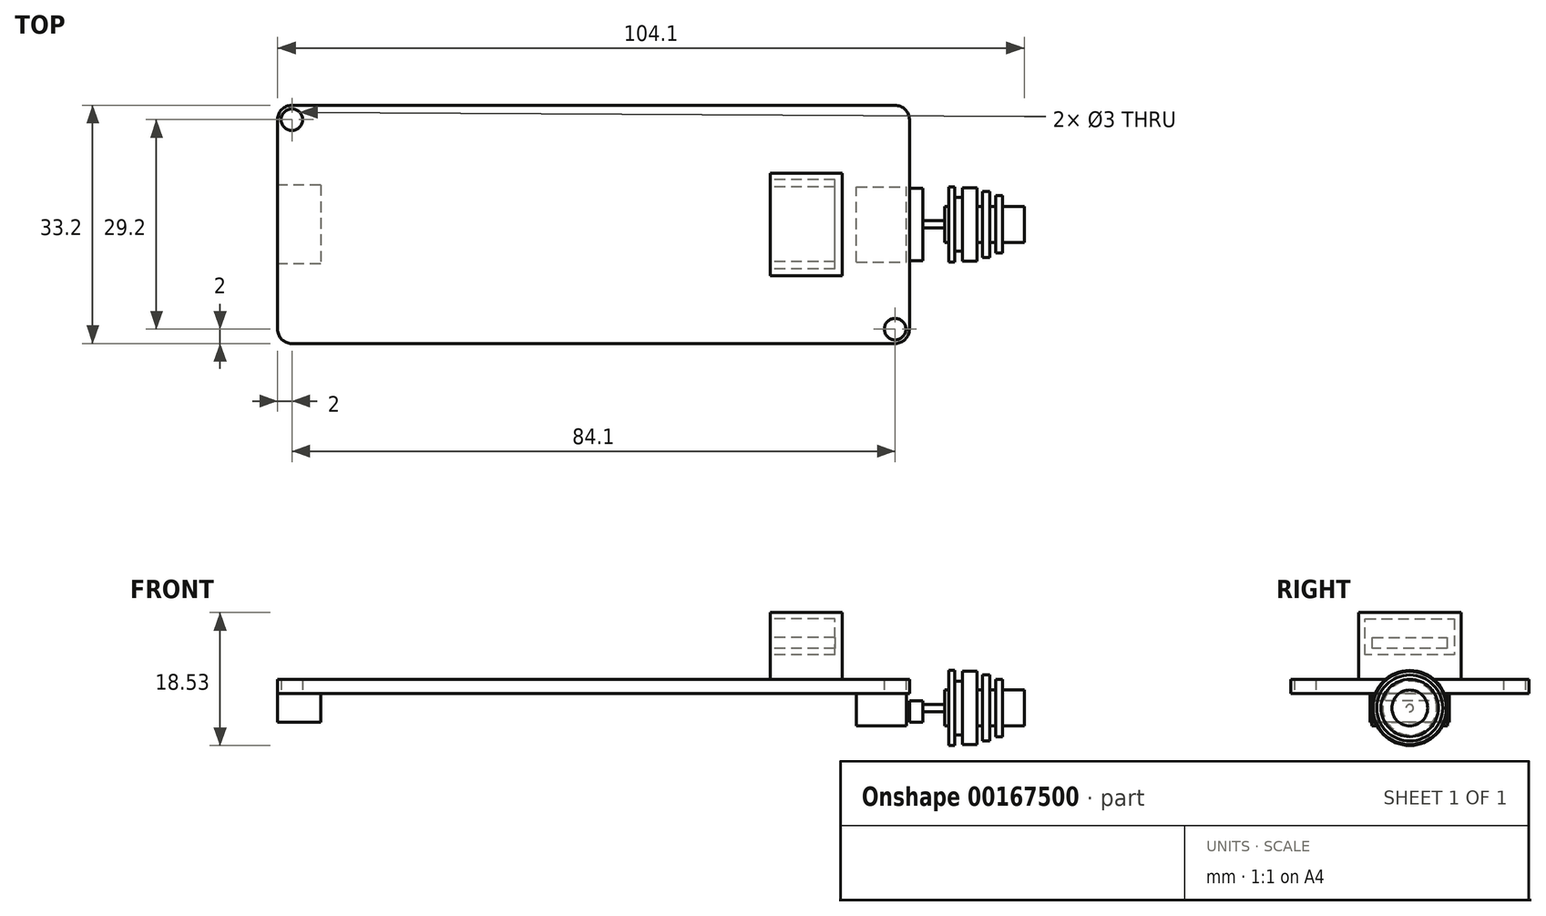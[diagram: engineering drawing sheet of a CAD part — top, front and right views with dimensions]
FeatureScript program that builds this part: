
annotation { "Feature Type Name" : "Feature", "Feature Type Description" : "" }
export const myFeature = defineFeature(function(context is Context, id is Id, definition is map)
    precondition{}
    {
        {
            var Q0;
            Q0=qCreatedBy(makeId("Top.planeOp"),FACE);
            var sketch = newSketch(context, id + "F0", { "sketchPlane" : qUnion([Q0])});
            skLineSegment(sketch, "E0.bottom", {"start": v(2, 0) * mm, "end": v(86.1, 0) * mm});
            skLineSegment(sketch, "E0.top", {"start": v(2, -33.2) * mm, "end": v(86.1, -33.2) * mm});
            skLineSegment(sketch, "E0.left", {"start": v(0, -2) * mm, "end": v(0, -31.2) * mm});
            skLineSegment(sketch, "E0.right", {"start": v(88.1, -2) * mm, "end": v(88.1, -31.2) * mm});
            skPoint(sketch, "E1.visualSharp", {"position": v(88.1, 0) * mm});
            skArc(sketch, "E1.filletArc", {"start": v(88.1, -2) * mm, "mid": v(87.51, -0.59) * mm, "end": v(86.1, 0) * mm});
            skPoint(sketch, "E2.visualSharp", {"position": v(88.1, -33.2) * mm});
            skArc(sketch, "E2.filletArc", {"start": v(86.1, -33.2) * mm, "mid": v(87.51, -32.61) * mm, "end": v(88.1, -31.2) * mm});
            skPoint(sketch, "E3.visualSharp", {"position": v(0, -33.2) * mm});
            skArc(sketch, "E3.filletArc", {"start": v(0, -31.2) * mm, "mid": v(0.59, -32.61) * mm, "end": v(2, -33.2) * mm});
            skPoint(sketch, "E4.visualSharp", {"position": v(0, 0) * mm});
            skArc(sketch, "E4.filletArc", {"start": v(2, 0) * mm, "mid": v(0.59, -0.59) * mm, "end": v(0, -2) * mm});
            skCircle(sketch, "E5", {"center": v(2, -2) * mm, "radius": 1.5 * mm});
            skCircle(sketch, "E6", {"center": v(86.1, -31.2) * mm, "radius": 1.5 * mm});
            skLineSegment(sketch, "E7", {"start": v(0, -16.6) * mm, "end": v(88.1, -16.6) * mm, "construction": true});
            skLineSegment(sketch, "E8", {"start": v(44.05, 0) * mm, "end": v(44.05, -33.2) * mm, "construction": true});
            skSolve(sketch);
        }
        {
            var Q0;
            Q0=makeQuery(id+"F0.imprint","IMPRINT",FACE,{"disambiguationData":[TD([[makeQuery(id+"F0.imprint","IMPRINT",EDGE,{"derivedFrom":sQuery(id+"F0.wireOp",EDGE,"E0.bottom")}),-1.0]])]});
            extrude(context, id + "F1", {"entities" : qUnion([Q0]), "depth" : 2 * mm});
        }
        {
            var Q0;
            Q0=makeQuery(id+"F1.opExtrude","CAP_FACE",FACE,{"disambiguationData":[OSD([sQuery(id+"F0.wireOp",EDGE,"E0.bottom"),sQuery(id+"F0.wireOp",EDGE,"E0.top"),sQuery(id+"F0.wireOp",EDGE,"E0.left"),sQuery(id+"F0.wireOp",EDGE,"E0.right"),sQuery(id+"F0.wireOp",EDGE,"E1.filletArc"),sQuery(id+"F0.wireOp",EDGE,"E2.filletArc"),sQuery(id+"F0.wireOp",EDGE,"E3.filletArc"),sQuery(id+"F0.wireOp",EDGE,"E4.filletArc"),sQuery(id+"F0.wireOp",EDGE,"E5"),sQuery(id+"F0.wireOp",EDGE,"E6")])],"isStart":false});
            var sketch = newSketch(context, id + "F2", { "sketchPlane" : qUnion([Q0])});
            skLineSegment(sketch, "E9.bottom", {"start": v(68.7, -9.45) * mm, "end": v(78.7, -9.45) * mm});
            skLineSegment(sketch, "E9.top", {"start": v(68.7, -23.75) * mm, "end": v(78.7, -23.75) * mm});
            skLineSegment(sketch, "E9.left", {"start": v(68.7, -9.45) * mm, "end": v(68.7, -23.75) * mm});
            skLineSegment(sketch, "E9.right", {"start": v(78.7, -9.45) * mm, "end": v(78.7, -23.75) * mm});
            skPoint(sketch, "E10", {"position": v(78.7, -16.6) * mm});
            skSolve(sketch);
        }
        {
            var Q0;
            Q0=makeQuery(id+"F2.imprint","IMPRINT",FACE,{"disambiguationData":[TD([[makeQuery(id+"F2.imprint","IMPRINT",EDGE,{"derivedFrom":sQuery(id+"F2.wireOp",EDGE,"E9.bottom")}),-1.0]])]});
            extrude(context, id + "F3", {"entities" : qUnion([Q0]), "depth" : 9.3 * mm});
        }
        {
            var Q0;
            Q0=makeQuery(id+"F3.opExtrude","SWEPT_FACE",FACE,{"disambiguationData":[OSD([sQuery(id+"F2.wireOp",EDGE,"E9.left")])]});
            var sketch = newSketch(context, id + "F4", { "sketchPlane" : qUnion([Q0])});
            skLineSegment(sketch, "E11.0.0", {"start": v(11.4, 7.8) * mm, "end": v(11.4, 6.3) * mm});
            skLineSegment(sketch, "E12.0.0", {"start": v(22.83, 10.4) * mm, "end": v(10.38, 10.4) * mm});
            skLineSegment(sketch, "E12.0.1", {"start": v(10.38, 10.4) * mm, "end": v(10.38, 5.4) * mm});
            skLineSegment(sketch, "E12.0.2", {"start": v(10.38, 5.4) * mm, "end": v(22.83, 5.4) * mm});
            skLineSegment(sketch, "E12.0.3", {"start": v(22.83, 5.4) * mm, "end": v(22.83, 10.4) * mm});
            skLineSegment(sketch, "E11.0.1", {"start": v(11.4, 6.3) * mm, "end": v(21.8, 6.3) * mm});
            skLineSegment(sketch, "E11.0.2", {"start": v(21.8, 6.3) * mm, "end": v(21.8, 7.8) * mm});
            skLineSegment(sketch, "E11.0.3", {"start": v(21.8, 7.8) * mm, "end": v(11.4, 7.8) * mm});
            skLineSegment(sketch, "E13.0", {"start": v(9.45, 11.3) * mm, "end": v(23.75, 11.3) * mm, "construction": true});
            skLineSegment(sketch, "E14.0", {"start": v(9.45, 11.3) * mm, "end": v(9.45, 2) * mm, "construction": true});
            skLineSegment(sketch, "E15.0", {"start": v(23.75, 11.3) * mm, "end": v(23.75, 2) * mm, "construction": true});
            skLineSegment(sketch, "E16.0", {"start": v(9.45, 2) * mm, "end": v(23.75, 2) * mm, "construction": true});
            skSolve(sketch);
        }
        {
            var Q0;
            Q0=makeQuery(id+"F4.imprint","IMPRINT",FACE,{"disambiguationData":[TD([[makeQuery(id+"F4.imprint","IMPRINT",EDGE,{"derivedFrom":sQuery(id+"F4.wireOp",EDGE,"E11.0.0")}),-1.0]])]});
            extrude(context, id + "F5", {"entities" : qUnion([Q0]), "operationType" : NewBodyOperationType.REMOVE, "oppositeDirection" : true, "depth" : 9 * mm});
        }
        {
            var Q0;
            Q0=makeQuery(id+"F1.opExtrude","CAP_FACE",FACE,{"disambiguationData":[OSD([sQuery(id+"F0.wireOp",EDGE,"E0.bottom"),sQuery(id+"F0.wireOp",EDGE,"E0.top"),sQuery(id+"F0.wireOp",EDGE,"E0.left"),sQuery(id+"F0.wireOp",EDGE,"E0.right"),sQuery(id+"F0.wireOp",EDGE,"E1.filletArc"),sQuery(id+"F0.wireOp",EDGE,"E2.filletArc"),sQuery(id+"F0.wireOp",EDGE,"E3.filletArc"),sQuery(id+"F0.wireOp",EDGE,"E4.filletArc"),sQuery(id+"F0.wireOp",EDGE,"E5"),sQuery(id+"F0.wireOp",EDGE,"E6")])],"isStart":true});
            var sketch = newSketch(context, id + "F6", { "sketchPlane" : qUnion([Q0])});
            skLineSegment(sketch, "E17.bottom", {"start": v(80.7, 21.85) * mm, "end": v(87.7, 21.85) * mm});
            skLineSegment(sketch, "E17.top", {"start": v(80.7, 11.35) * mm, "end": v(87.7, 11.35) * mm});
            skLineSegment(sketch, "E17.left", {"start": v(80.7, 21.85) * mm, "end": v(80.7, 11.35) * mm});
            skLineSegment(sketch, "E17.right", {"start": v(87.7, 21.85) * mm, "end": v(87.7, 11.35) * mm});
            skPoint(sketch, "E18", {"position": v(87.7, 16.6) * mm});
            skLineSegment(sketch, "E19.bottom", {"start": v(87.7, 21.65) * mm, "end": v(90, 21.65) * mm});
            skLineSegment(sketch, "E19.top", {"start": v(87.7, 11.55) * mm, "end": v(90, 11.55) * mm});
            skLineSegment(sketch, "E19.left", {"start": v(87.7, 21.65) * mm, "end": v(87.7, 11.55) * mm});
            skLineSegment(sketch, "E19.right", {"start": v(90, 21.65) * mm, "end": v(90, 11.55) * mm});
            skLineSegment(sketch, "E20", {"start": v(87.7, 16.6) * mm, "end": v(100.65, 16.6) * mm, "construction": true});
            skLineSegment(sketch, "E21", {"start": v(93, 17.1) * mm, "end": v(93, 19.1) * mm});
            skLineSegment(sketch, "E22", {"start": v(93, 19.1) * mm, "end": v(93.6, 19.1) * mm});
            skLineSegment(sketch, "E23", {"start": v(93.6, 19.1) * mm, "end": v(93.6, 21.82) * mm});
            skLineSegment(sketch, "E24", {"start": v(93.6, 21.82) * mm, "end": v(94.4, 21.82) * mm});
            skLineSegment(sketch, "E25", {"start": v(94.4, 21.82) * mm, "end": v(94.4, 20.35) * mm});
            skLineSegment(sketch, "E26", {"start": v(94.4, 20.35) * mm, "end": v(95.5, 20.35) * mm});
            skLineSegment(sketch, "E27", {"start": v(95.5, 20.35) * mm, "end": v(95.5, 21.7) * mm});
            skLineSegment(sketch, "E28", {"start": v(95.5, 21.7) * mm, "end": v(97.5, 21.7) * mm});
            skLineSegment(sketch, "E29", {"start": v(97.5, 21.7) * mm, "end": v(97.5, 19.1) * mm});
            skLineSegment(sketch, "E30", {"start": v(97.5, 19.1) * mm, "end": v(98.3, 19.1) * mm});
            skLineSegment(sketch, "E31", {"start": v(98.3, 19.1) * mm, "end": v(98.3, 21.2) * mm});
            skLineSegment(sketch, "E32", {"start": v(98.3, 21.2) * mm, "end": v(99.3, 21.2) * mm});
            skLineSegment(sketch, "E33", {"start": v(99.3, 21.2) * mm, "end": v(99.3, 19.1) * mm});
            skLineSegment(sketch, "E34", {"start": v(99.3, 19.1) * mm, "end": v(100.1, 19.1) * mm});
            skLineSegment(sketch, "E35", {"start": v(100.1, 19.1) * mm, "end": v(100.1, 20.6) * mm});
            skLineSegment(sketch, "E36", {"start": v(100.1, 20.6) * mm, "end": v(101.1, 20.6) * mm});
            skLineSegment(sketch, "E37", {"start": v(101.1, 20.6) * mm, "end": v(101.1, 19.1) * mm});
            skLineSegment(sketch, "E38", {"start": v(101.1, 19.1) * mm, "end": v(104.1, 19.1) * mm});
            skLineSegment(sketch, "E39", {"start": v(104.1, 19.1) * mm, "end": v(104.1, 16.6) * mm});
            skLineSegment(sketch, "E40", {"start": v(90, 16.6) * mm, "end": v(104.1, 16.6) * mm});
            skLineSegment(sketch, "E41", {"start": v(93, 17.1) * mm, "end": v(90, 17.1) * mm});
            skLineSegment(sketch, "E42.bottom", {"start": v(6, 11.1) * mm, "end": v(0, 11.1) * mm});
            skLineSegment(sketch, "E42.top", {"start": v(6, 22.1) * mm, "end": v(0, 22.1) * mm});
            skLineSegment(sketch, "E42.left", {"start": v(6, 11.1) * mm, "end": v(6, 22.1) * mm});
            skLineSegment(sketch, "E42.right", {"start": v(0, 11.1) * mm, "end": v(0, 22.1) * mm});
            skPoint(sketch, "E43", {"position": v(6, 16.6) * mm});
            skSolve(sketch);
        }
        {
            var Q0;
            Q0=makeQuery(id+"F6.imprint","IMPRINT",FACE,{"disambiguationData":[TD([[makeQuery(id+"F6.imprint","IMPRINT",EDGE,{"derivedFrom":sQuery(id+"F6.wireOp",EDGE,"E17.bottom")}),-1.0]])]});
            extrude(context, id + "F7", {"entities" : qUnion([Q0]), "depth" : 4.5 * mm});
        }
        {
            var Q0;
            {var subQ5=sQuery(id+"F6.wireOp",EDGE,"E19.right");Q0=makeQuery(id+"F6.imprint","IMPRINT",FACE,{"disambiguationData":[TD([[makeQuery(id+"F6.imprint","IMPRINT",EDGE,{"derivedFrom":subQ5}),-1.0]])]});}
            var Q1;
            {var subQ0=sQuery(id+"F6.wireOp",EDGE,"E19.left");Q1=makeQuery(id+"F6.imprint","IMPRINT",FACE,{"disambiguationData":[TD([[makeQuery(id+"F6.imprint","IMPRINT",EDGE,{"derivedFrom":subQ0}),1.0]])]});}
            extrude(context, id + "F8", {"entities" : qUnion([Q0, Q1]), "depth" : 4 * mm, "hasSecondDirection" : true, "secondDirectionOppositeDirection" : false, "secondDirectionDepth" : 1 * mm});
        }
        {
            var Q0;
            Q0=makeQuery(id+"F6.imprint","IMPRINT",FACE,{"disambiguationData":[TD([[makeQuery(id+"F6.imprint","IMPRINT",EDGE,{"derivedFrom":sQuery(id+"F6.wireOp",EDGE,"E21")}),-1.0]])]});
            var Q1;
            Q1=sQuery(id+"F6.wireOp",EDGE,"E20");
            revolve(context, id + "F9", {"entities" : qUnion([Q0]), "axis" : qUnion([Q1]), "revolveType" : RevolveType.FULL});
        }
        {
            var Q0;
            Q0=makeQuery(id+"F9.opRevolve","SWEPT_BODY",BODY,{"disambiguationData":[OSD([sQuery(id+"F6.wireOp",EDGE,"E21"),sQuery(id+"F6.wireOp",EDGE,"E22"),sQuery(id+"F6.wireOp",EDGE,"E23"),sQuery(id+"F6.wireOp",EDGE,"E24"),sQuery(id+"F6.wireOp",EDGE,"E25"),sQuery(id+"F6.wireOp",EDGE,"E26"),sQuery(id+"F6.wireOp",EDGE,"E27"),sQuery(id+"F6.wireOp",EDGE,"E28"),sQuery(id+"F6.wireOp",EDGE,"E29"),sQuery(id+"F6.wireOp",EDGE,"E30"),sQuery(id+"F6.wireOp",EDGE,"E31"),sQuery(id+"F6.wireOp",EDGE,"E32"),sQuery(id+"F6.wireOp",EDGE,"E33"),sQuery(id+"F6.wireOp",EDGE,"E34"),sQuery(id+"F6.wireOp",EDGE,"E35"),sQuery(id+"F6.wireOp",EDGE,"E36"),sQuery(id+"F6.wireOp",EDGE,"E37"),sQuery(id+"F6.wireOp",EDGE,"E38"),sQuery(id+"F6.wireOp",EDGE,"E39"),sQuery(id+"F6.wireOp",EDGE,"E40")])]});
            transform(context, id + "F10", {"entities" : qUnion([Q0]), "transformType" : TransformType.TRANSLATION_3D, "dx" : 0 * mm, "dy" : 0 * mm, "dz" : -2 * mm, "makeCopy" : false});
        }
        {
            var Q0;
            Q0=makeQuery(id+"F6.imprint","IMPRINT",FACE,{"disambiguationData":[TD([[makeQuery(id+"F6.imprint","IMPRINT",EDGE,{"derivedFrom":sQuery(id+"F6.wireOp",EDGE,"E42.bottom")}),-1.0]])]});
            extrude(context, id + "F11", {"entities" : qUnion([Q0]), "depth" : 4 * mm});
        }
    });
